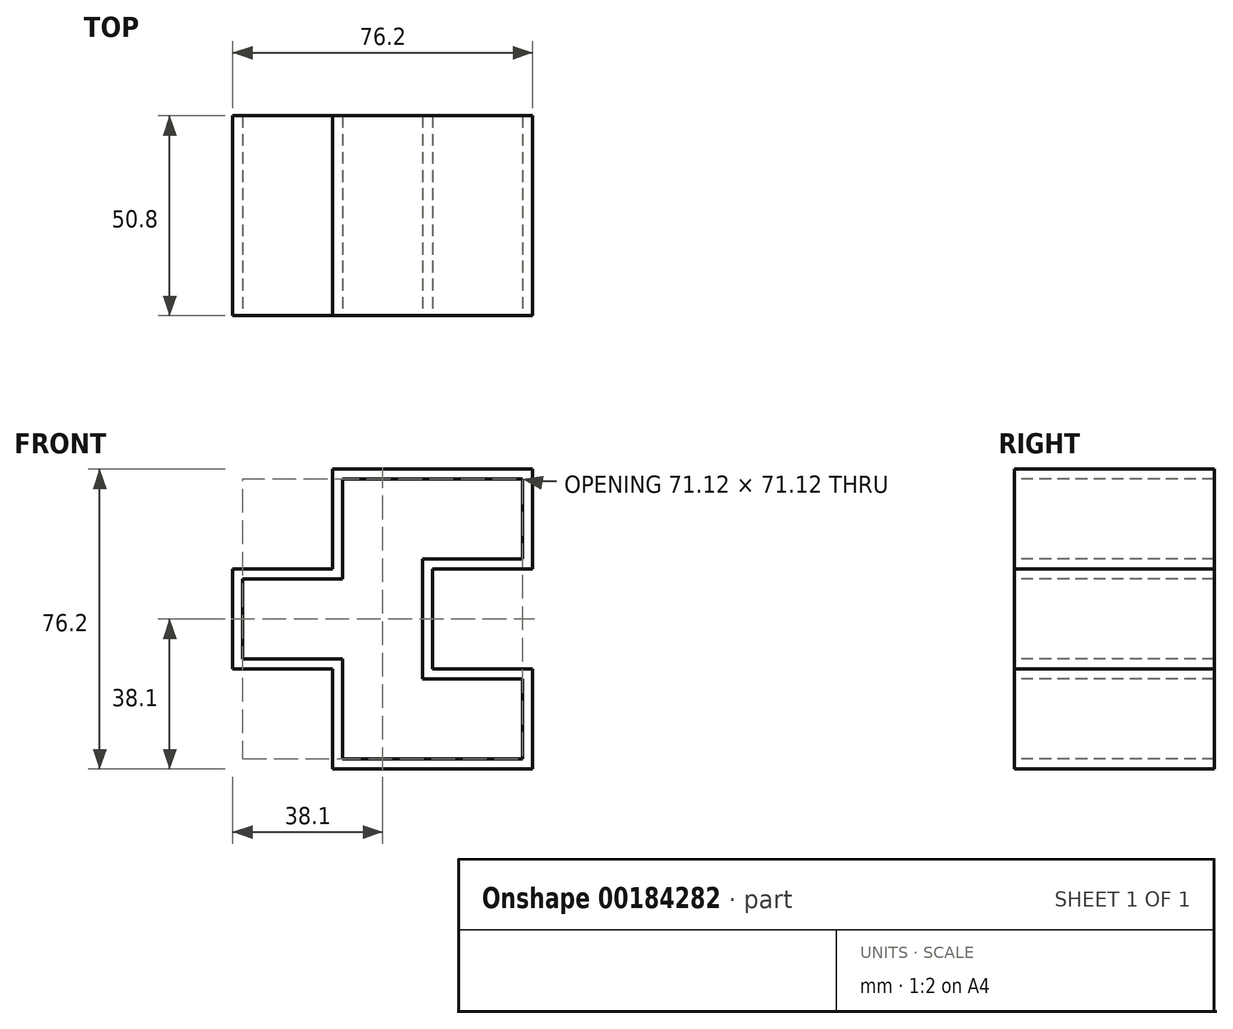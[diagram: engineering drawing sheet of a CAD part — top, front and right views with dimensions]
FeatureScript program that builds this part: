
annotation { "Feature Type Name" : "Feature", "Feature Type Description" : "" }
export const myFeature = defineFeature(function(context is Context, id is Id, definition is map)
    precondition{}
    {
        {
            var Q0;
            Q0=qCreatedBy(makeId("Front.planeOp"),FACE);
            var sketch = newSketch(context, id + "F0", { "sketchPlane" : qUnion([Q0])});
            skLineSegment(sketch, "E0", {"start": v(0, 0) * mm, "end": v(0, 25.4) * mm});
            skLineSegment(sketch, "E1", {"start": v(0, 25.4) * mm, "end": v(25.4, 25.4) * mm});
            skLineSegment(sketch, "E2", {"start": v(25.4, 25.4) * mm, "end": v(25.4, 50.8) * mm});
            skLineSegment(sketch, "E3", {"start": v(25.4, 50.8) * mm, "end": v(76.2, 50.8) * mm});
            skLineSegment(sketch, "E4", {"start": v(76.2, 50.8) * mm, "end": v(76.2, 25.4) * mm});
            skLineSegment(sketch, "E5", {"start": v(76.2, 25.4) * mm, "end": v(50.8, 25.4) * mm});
            skLineSegment(sketch, "E6", {"start": v(50.8, 25.4) * mm, "end": v(50.8, 0) * mm});
            skLineSegment(sketch, "E7", {"start": v(50.8, 0) * mm, "end": v(76.2, 0) * mm});
            skLineSegment(sketch, "E8", {"start": v(76.2, 0) * mm, "end": v(76.2, -25.4) * mm});
            skLineSegment(sketch, "E9", {"start": v(76.2, -25.4) * mm, "end": v(25.4, -25.4) * mm});
            skLineSegment(sketch, "E10", {"start": v(25.4, -25.4) * mm, "end": v(25.4, 0) * mm});
            skLineSegment(sketch, "E11", {"start": v(25.4, 0) * mm, "end": v(0, 0) * mm});
            skSolve(sketch);
        }
        {
            var Q0;
            Q0=makeQuery(id+"F0.imprint","IMPRINT",FACE,{"disambiguationData":[TD([[makeQuery(id+"F0.imprint","IMPRINT",EDGE,{"derivedFrom":sQuery(id+"F0.wireOp",EDGE,"E0")}),-1.0]])]});
            var sketch = newSketch(context, id + "F1", { "sketchPlane" : qUnion([Q0])});
            skLineSegment(sketch, "E12.0", {"start": v(27.94, 22.86) * mm, "end": v(27.94, 48.26) * mm});
            skLineSegment(sketch, "E12.1", {"start": v(48.26, -2.54) * mm, "end": v(73.66, -2.54) * mm});
            skLineSegment(sketch, "E12.2", {"start": v(48.26, 27.94) * mm, "end": v(48.26, -2.54) * mm});
            skLineSegment(sketch, "E12.3", {"start": v(73.66, 27.94) * mm, "end": v(48.26, 27.94) * mm});
            skLineSegment(sketch, "E12.4", {"start": v(73.66, 48.26) * mm, "end": v(73.66, 27.94) * mm});
            skLineSegment(sketch, "E12.5", {"start": v(73.66, -2.54) * mm, "end": v(73.66, -22.86) * mm});
            skLineSegment(sketch, "E12.6", {"start": v(27.94, 48.26) * mm, "end": v(73.66, 48.26) * mm});
            skLineSegment(sketch, "E12.7", {"start": v(73.66, -22.86) * mm, "end": v(27.94, -22.86) * mm});
            skLineSegment(sketch, "E12.8", {"start": v(27.94, -22.86) * mm, "end": v(27.94, 2.54) * mm});
            skLineSegment(sketch, "E12.9", {"start": v(27.94, 2.54) * mm, "end": v(2.54, 2.54) * mm});
            skLineSegment(sketch, "E12.10", {"start": v(2.54, 2.54) * mm, "end": v(2.54, 22.86) * mm});
            skLineSegment(sketch, "E12.11", {"start": v(2.54, 22.86) * mm, "end": v(27.94, 22.86) * mm});
            skSolve(sketch);
        }
        {
            var Q0;
            Q0=makeQuery(id+"F1.imprint","IMPRINT",FACE,{"disambiguationData":[TD([[makeQuery(id+"F1.imprint","IMPRINT",EDGE,{"derivedFrom":sQuery(id+"F1.wireOp",EDGE,"E12.0")}),1.0]])]});
            extrude(context, id + "F2", {"entities" : qUnion([Q0]), "oppositeDirection" : true, "depth" : 50.8 * mm});
        }
    });
